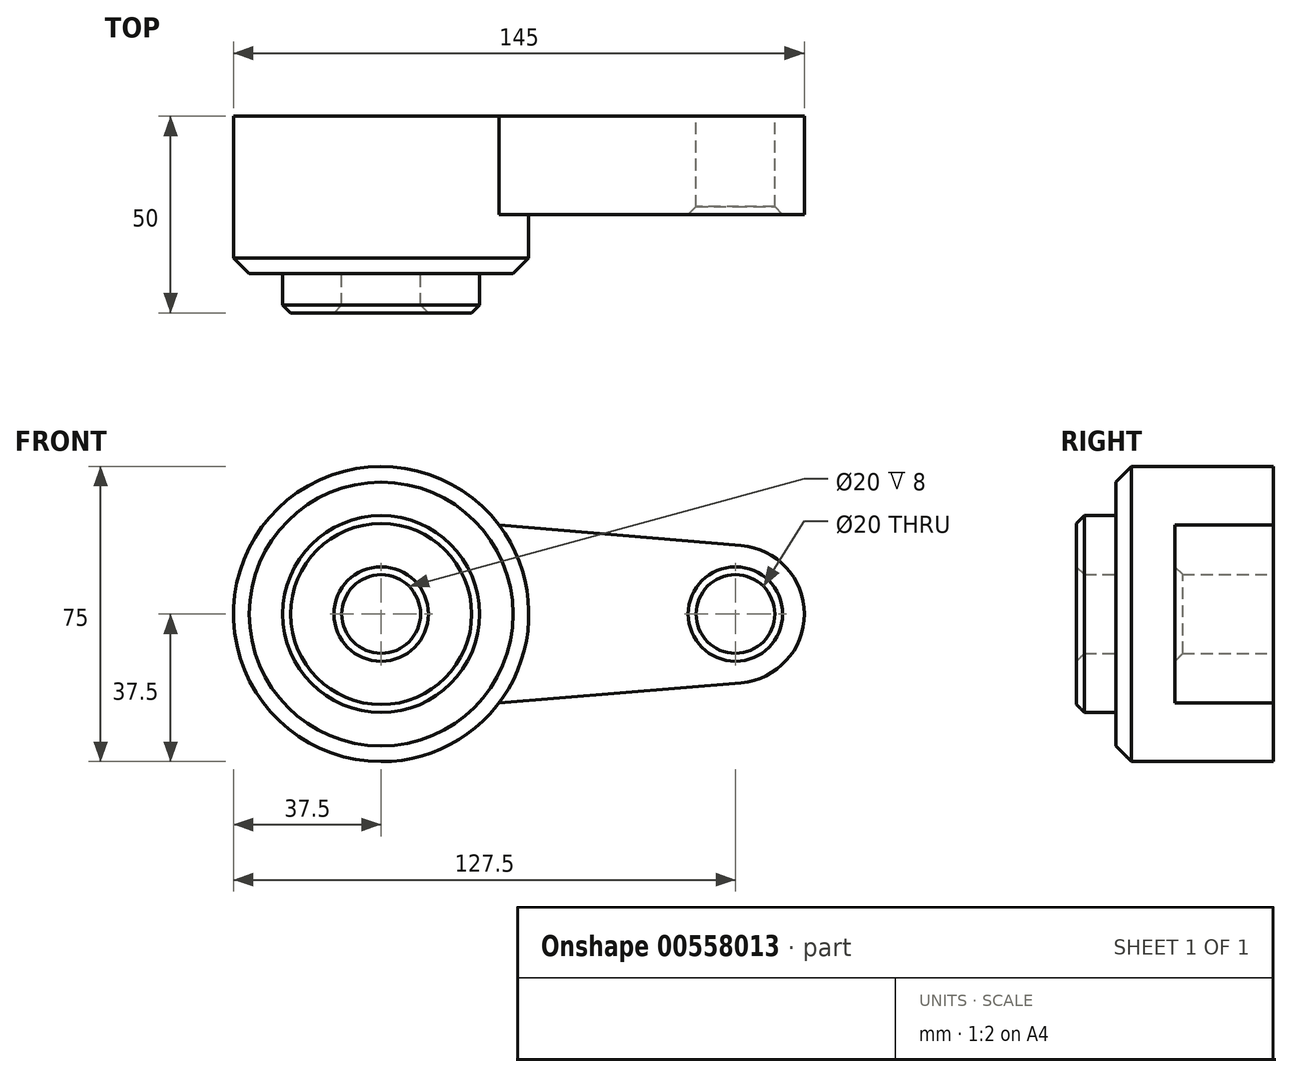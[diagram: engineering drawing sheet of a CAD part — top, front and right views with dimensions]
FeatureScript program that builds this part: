
annotation { "Feature Type Name" : "Feature", "Feature Type Description" : "" }
export const myFeature = defineFeature(function(context is Context, id is Id, definition is map)
    precondition{}
    {
        {
            var Q0;
            Q0=qCreatedBy(makeId("Front.planeOp"),FACE);
            var sketch = newSketch(context, id + "F0", { "sketchPlane" : qUnion([Q0])});
            skCircle(sketch, "E0", {"center": v(0, 0) * mm, "radius": 25 * mm});
            skCircle(sketch, "E1", {"center": v(90, 0) * mm, "radius": 17.5 * mm});
            skLineSegment(sketch, "E2", {"start": v(2.08, 24.91) * mm, "end": v(91.46, 17.44) * mm});
            skLineSegment(sketch, "E3", {"start": v(2.08, -24.91) * mm, "end": v(91.46, -17.44) * mm});
            skCircle(sketch, "E4", {"center": v(0, 0) * mm, "radius": 10 * mm});
            skCircle(sketch, "E5", {"center": v(90, 0) * mm, "radius": 10 * mm});
            skSolve(sketch);
        }
        {
            var Q0;
            Q0=qSketchRegion(id+"F0",true);
            extrude(context, id + "F1", {"entities" : qUnion([Q0]), "depth" : 25 * mm});
        }
        {
            var Q0;
            Q0=makeQuery(id+"F0.imprint","IMPRINT",FACE,{"disambiguationData":[TD([[makeQuery(id+"F0.imprint","IMPRINT",EDGE,{"derivedFrom":sQuery(id+"F0.wireOp",EDGE,"E4")}),-1.0]])]});
            extrude(context, id + "F2", {"entities" : qUnion([Q0]), "operationType" : NewBodyOperationType.ADD, "depth" : 50 * mm});
        }
        {
            var Q0;
            Q0=makeQuery(id+"F2.opExtrude","CAP_EDGE",EDGE,{"disambiguationData":[OSD([sQuery(id+"F0.wireOp",EDGE,"E0")])],"isStart":false});
            var Q1;
            Q1=makeQuery(id+"F2.opExtrude","CAP_EDGE",EDGE,{"disambiguationData":[OSD([sQuery(id+"F0.wireOp",EDGE,"E4")])],"isStart":false});
            var Q2;
            Q2=makeQuery(id+"F1.opExtrude","CAP_EDGE",EDGE,{"disambiguationData":[OSD([sQuery(id+"F0.wireOp",EDGE,"E5")])],"isStart":false});
            chamfer(context, id + "F3", {"entities" : qUnion([Q0, Q1, Q2]), "width" : 2 * mm, "tangentPropagation" : true});
        }
        {
            var Q0;
            Q0=qCreatedBy(makeId("Front.planeOp"),FACE);
            var sketch = newSketch(context, id + "F4", { "sketchPlane" : qUnion([Q0])});
            skCircle(sketch, "E6", {"center": v(0, 0) * mm, "radius": 37.5 * mm});
            skSolve(sketch);
        }
        {
            var Q0;
            Q0 = qSketchRegion(id + "F4", true);
            extrude(context, id + "F5", {"entities" : qUnion([Q0]), "operationType" : NewBodyOperationType.ADD, "depth" : 40 * mm, "offsetDistance" : 25 * mm});
        }
        {
            var Q0;
            Q0=makeQuery(id+"F5.opExtrude","CAP_EDGE",EDGE,{"disambiguationData":[OSD([sQuery(id+"F4.wireOp",EDGE,"E6")])],"isStart":false});
            chamfer(context, id + "F6", {"entities" : qUnion([Q0]), "width" : 4 * mm, "tangentPropagation" : true});
        }
    });
